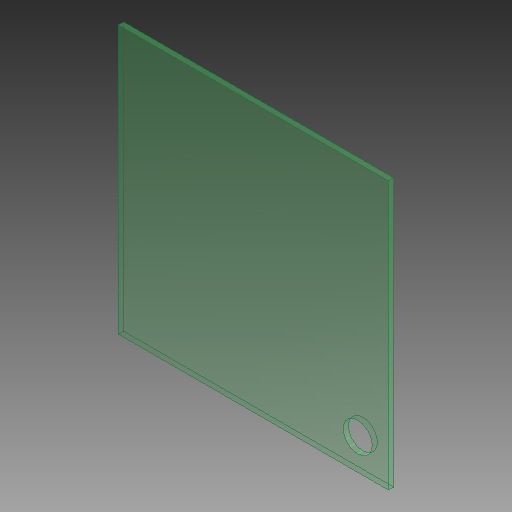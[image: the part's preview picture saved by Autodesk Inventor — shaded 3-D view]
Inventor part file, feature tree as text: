
AUTODESK INVENTOR PART (.ipt)
format: ipt  version: 2018.1 (Build 221171000, 171)  size: 118,272 bytes
history: native  units: mm
features: extrude x3, sketch x3
ambient origin geometry x8: Origin, YZ Plane, XZ Plane, XY Plane, X Axis, Y Axis, Z Axis, Center Point
bodies: Solid1 (feature_tree)
feature tree (6):
  extrude  "Extrusion1"  Depth=260.0mm
  extrude  "Extrusion3"  TaperAngle=0.0deg  [1 undecoded]
  extrude  "Extrusion4"  Depth=5.0mm
  sketch  "Sketch1"  dims[d0=258.0mm d1=260.0mm]
  sketch  "Sketch3"  dims[d2=5.0mm d3=0.0mm]
  sketch  "Sketch4"  dims[d12=29.5mm d13=29.5mm d14=28.0mm d15=5.0mm d16=0.0mm d17=25.0mm d18=22.5mm d19=132.5mm d20=16.0mm d21=25.0mm d22=45.0mm d23=16.0mm d24=132.5mm d25=5.0mm d26=0.0mm]
note: 1 required parameter value undecoded (feature->parameter linkage not recoverable at this tier; creation-order binding heuristic only, values carry confidence <= 0.55)
